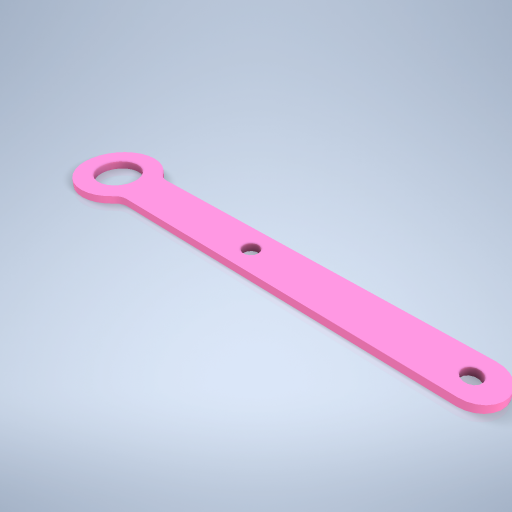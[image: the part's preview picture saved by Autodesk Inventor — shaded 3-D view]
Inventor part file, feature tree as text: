
AUTODESK INVENTOR PART (.ipt)
format: ipt  version: 2024.2 (Build 282272000, 272)  size: 268,288 bytes
history: native  units: mm
features: sketch x3, hole x2, extrude x1, fillet x1
ambient origin geometry x8: Origin, YZ Plane, XZ Plane, XY Plane, X Axis, Y Axis, Z Axis, Center Point
bodies: Volumenkörper1 (feature_tree)
feature tree (7):
  extrude  "Extrusion1"  Depth=6.0mm
  fillet  "Rundung1"  Radius=5.5mm
  hole  "Bohrung2"  [1 undecoded]
  hole  "Bohrung1"  [1 undecoded]
  sketch  "Skizze1"  dims[d1=6.0mm d4=6.0mm d5=5.5mm]
  sketch  "Skizze2"  dims[d6=3.0mm d7=50.0mm]
  sketch  "Skizze3"  dims[d8=1.0mm d9=0.0mm d10=2.0mm d11=2.2mm d12=8.0mm d13=6.0mm d14=2.5mm d15=90.0deg d16=11.8mm d17=20.594885mm d18=23.0mm d19=2.2mm d20=6.0mm d21=4.0mm d22=2.0mm d23=90.0deg d24=8.0mm d25=20.594885mm d26=49.5mm]
note: 2 required parameter values undecoded (feature->parameter linkage not recoverable at this tier; creation-order binding heuristic only, values carry confidence <= 0.55)
